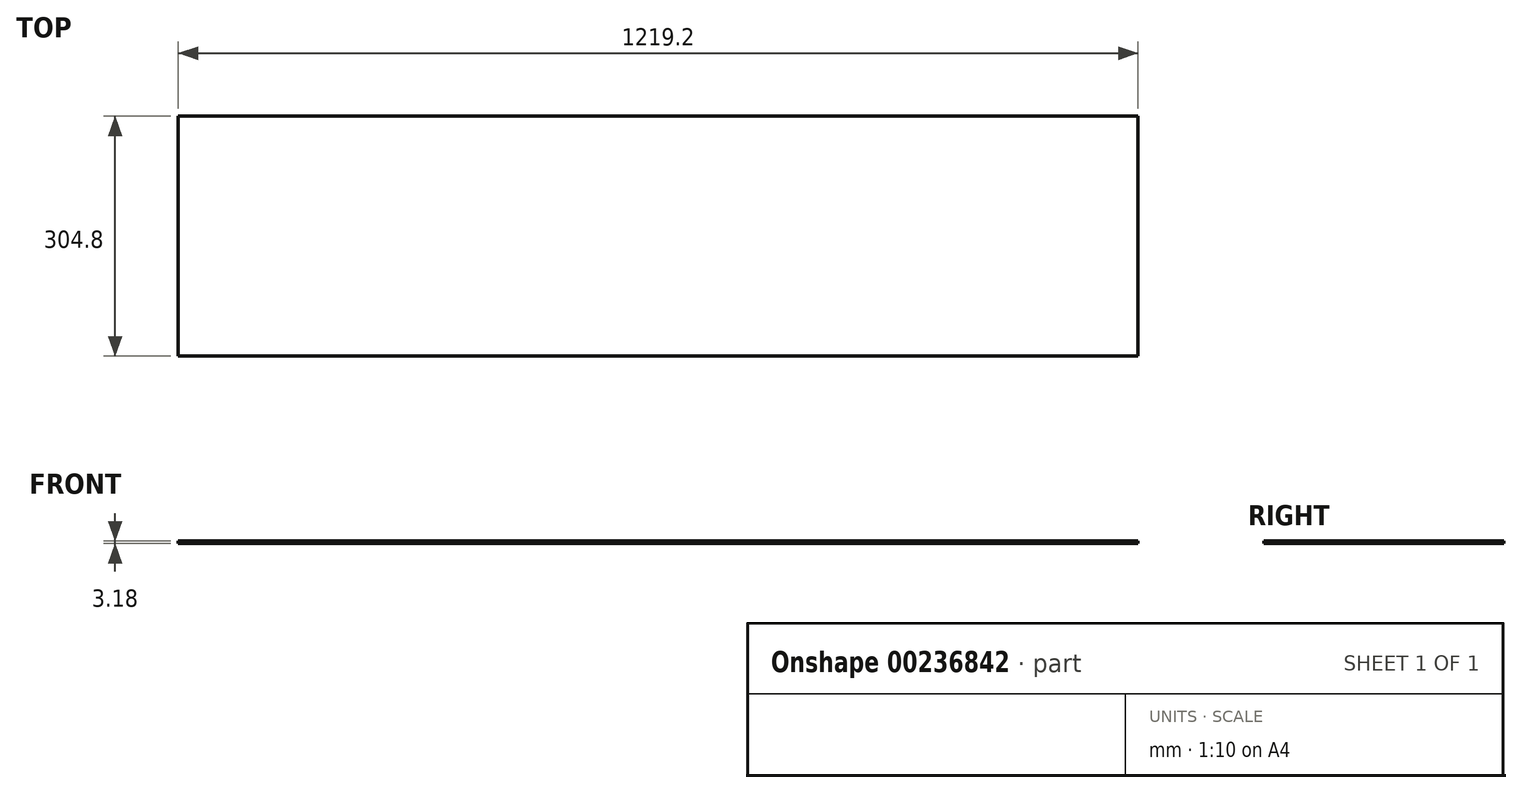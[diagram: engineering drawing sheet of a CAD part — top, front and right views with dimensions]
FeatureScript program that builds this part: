
annotation { "Feature Type Name" : "Feature", "Feature Type Description" : "" }
export const myFeature = defineFeature(function(context is Context, id is Id, definition is map)
    precondition{}
    {
        {
            var Q0;
            Q0=qCreatedBy(makeId("Top.planeOp"),FACE);
            var sketch = newSketch(context, id + "F0", { "sketchPlane" : qUnion([Q0])});
            skLineSegment(sketch, "E0.bottom", {"start": v(609.6, -152.4) * mm, "end": v(-609.6, -152.4) * mm});
            skLineSegment(sketch, "E0.top", {"start": v(609.6, 152.4) * mm, "end": v(-609.6, 152.4) * mm});
            skLineSegment(sketch, "E0.left", {"start": v(609.6, -152.4) * mm, "end": v(609.6, 152.4) * mm});
            skLineSegment(sketch, "E0.right", {"start": v(-609.6, -152.4) * mm, "end": v(-609.6, 152.4) * mm});
            skPoint(sketch, "E0.middle", {"position": v(0, 0) * mm});
            skSolve(sketch);
        }
        {
            var Q0;
            Q0=qSketchRegion(id+"F0",true);
            extrude(context, id + "F1", {"entities" : qUnion([Q0]), "endBound" : BoundingType.SYMMETRIC, "depth" : 3.17 * mm});
        }
    });
